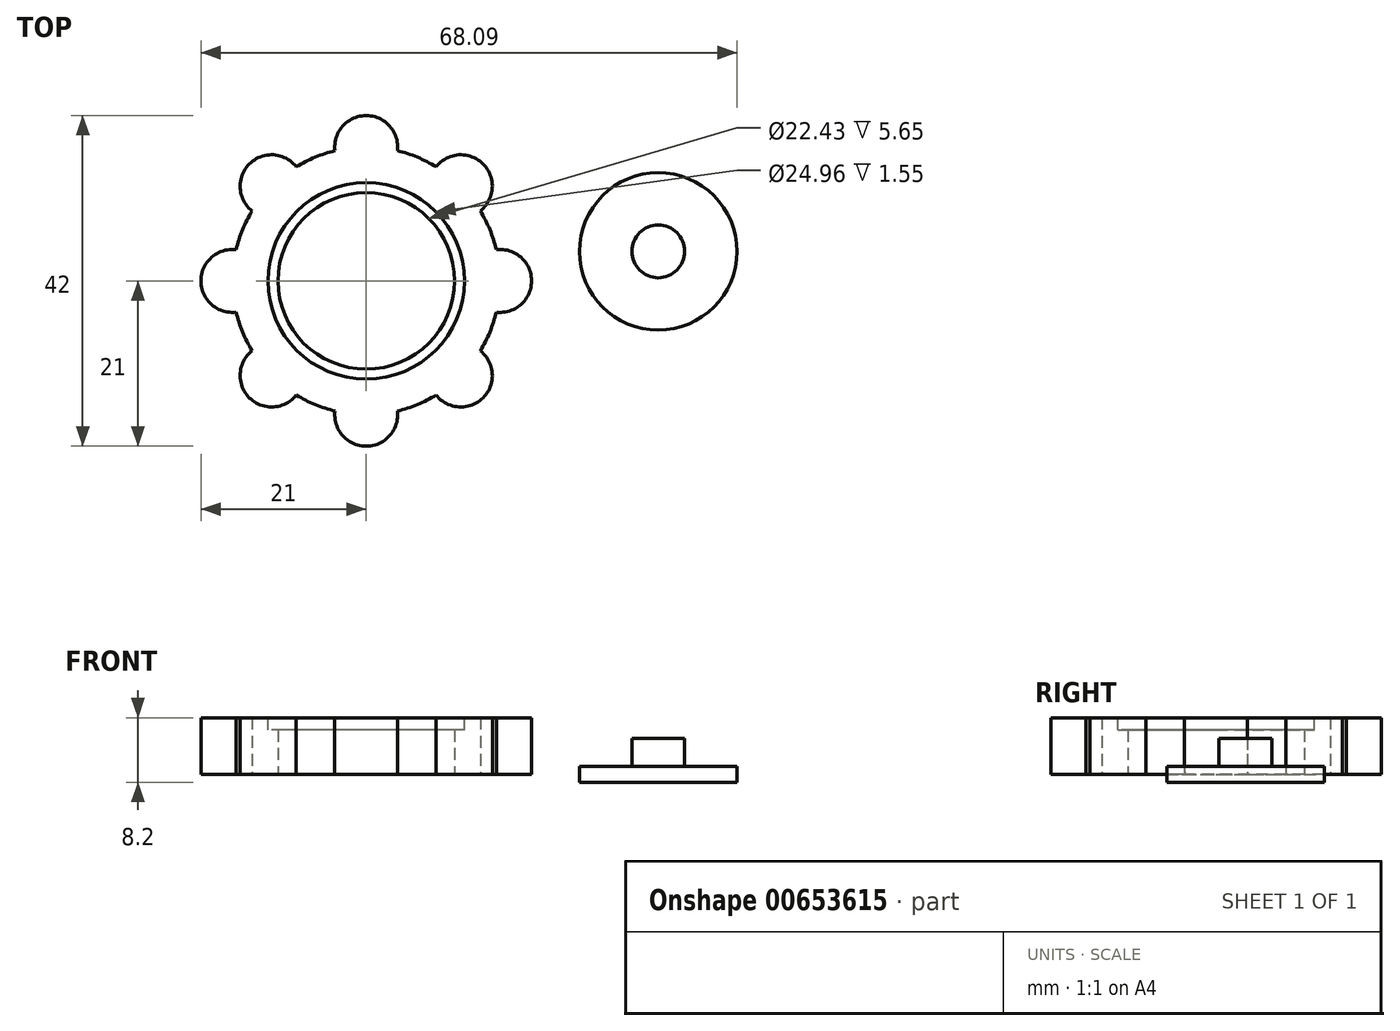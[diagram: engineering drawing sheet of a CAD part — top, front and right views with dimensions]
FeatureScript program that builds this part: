
annotation { "Feature Type Name" : "Feature", "Feature Type Description" : "" }
export const myFeature = defineFeature(function(context is Context, id is Id, definition is map)
    precondition{}
    {
        {
            var Q0;
            Q0=qCreatedBy(makeId("Top.planeOp"),FACE);
            var sketch = newSketch(context, id + "F0", { "sketchPlane" : qUnion([Q0])});
            skCircle(sketch, "E0", {"center": v(0, 0) * mm, "radius": 4.66 * mm});
            skCircle(sketch, "E1", {"center": v(0, 0) * mm, "radius": 11.21 * mm});
            skArc(sketch, "E2", {"start": v(-14.5, 8.88) * mm, "mid": v(-15.7, 6.5) * mm, "end": v(-16.53, 3.97) * mm});
            skArc(sketch, "E3", {"start": v(3.97, 16.53) * mm, "mid": v(0, 21) * mm, "end": v(-3.97, 16.53) * mm});
            skArc(sketch, "E4", {"start": v(-8.88, 14.5) * mm, "mid": v(-14.85, 14.85) * mm, "end": v(-14.5, 8.88) * mm});
            skArc(sketch, "E5", {"start": v(-16.53, 3.97) * mm, "mid": v(-21, 0) * mm, "end": v(-16.53, -3.97) * mm});
            skArc(sketch, "E6.MirrorC", {"start": v(-8.88, -14.5) * mm, "mid": v(-14.85, -14.85) * mm, "end": v(-14.5, -8.88) * mm});
            skArc(sketch, "E7.MirrorC", {"start": v(3.97, -16.53) * mm, "mid": v(0, -21) * mm, "end": v(-3.97, -16.53) * mm});
            skArc(sketch, "E8.MirrorC", {"start": v(8.88, 14.5) * mm, "mid": v(14.85, 14.85) * mm, "end": v(14.5, 8.88) * mm});
            skArc(sketch, "E9.MirrorC", {"start": v(16.53, 3.97) * mm, "mid": v(21, 0) * mm, "end": v(16.53, -3.97) * mm});
            skArc(sketch, "E10.MirrorC", {"start": v(8.88, -14.5) * mm, "mid": v(14.85, -14.85) * mm, "end": v(14.5, -8.88) * mm});
            skArc(sketch, "E11.trimOffspring", {"start": v(-16.53, -3.97) * mm, "mid": v(-15.7, -6.5) * mm, "end": v(-14.5, -8.88) * mm});
            skArc(sketch, "E12.trimOffspring", {"start": v(-8.88, -14.5) * mm, "mid": v(-6.5, -15.7) * mm, "end": v(-3.97, -16.53) * mm});
            skArc(sketch, "E13.trimOffspring", {"start": v(3.97, -16.53) * mm, "mid": v(6.5, -15.7) * mm, "end": v(8.88, -14.5) * mm});
            skArc(sketch, "E14.trimOffspring", {"start": v(14.5, -8.88) * mm, "mid": v(15.7, -6.5) * mm, "end": v(16.53, -3.97) * mm});
            skArc(sketch, "E15.trimOffspring", {"start": v(16.53, 3.97) * mm, "mid": v(15.7, 6.5) * mm, "end": v(14.5, 8.88) * mm});
            skArc(sketch, "E16.trimOffspring", {"start": v(8.88, 14.5) * mm, "mid": v(6.5, 15.7) * mm, "end": v(3.97, 16.53) * mm});
            skArc(sketch, "E17.trimOffspring", {"start": v(-3.97, 16.53) * mm, "mid": v(-6.5, 15.7) * mm, "end": v(-8.88, 14.5) * mm});
            skSolve(sketch);
        }
        {
            var Q0;
            Q0=makeQuery(id+"F0.imprint","IMPRINT",FACE,{"disambiguationData":[TD([[makeQuery(id+"F0.imprint","IMPRINT",EDGE,{"derivedFrom":sQuery(id+"F0.wireOp",EDGE,"E0")}),1.0]])]});
            var Q1;
            Q1=makeQuery(id+"F0.imprint","IMPRINT",FACE,{"disambiguationData":[TD([[makeQuery(id+"F0.imprint","IMPRINT",EDGE,{"derivedFrom":sQuery(id+"F0.wireOp",EDGE,"E1")}),-1.0]])]});
            extrude(context, id + "F1", {"entities" : qUnion([Q0, Q1]), "depth" : 7.2 * mm, "offsetDistance" : 25 * mm});
        }
        {
            var Q0;
            Q0=makeQuery(id+"F1.opExtrude","CAP_FACE",FACE,{"disambiguationData":[OSD([sQuery(id+"F0.wireOp",EDGE,"E1"),sQuery(id+"F0.wireOp",EDGE,"E2")])],"isStart":false});
            var sketch = newSketch(context, id + "F2", { "sketchPlane" : qUnion([Q0])});
            skCircle(sketch, "E18", {"center": v(0, 0) * mm, "radius": 12.48 * mm});
            skSolve(sketch);
        }
        {
            var Q0;
            Q0=makeQuery(id+"F2.imprint","IMPRINT",FACE,{"disambiguationData":[TD([[makeQuery(id+"F2.imprint","IMPRINT",EDGE,{"derivedFrom":sQuery(id+"F2.wireOp",EDGE,"E18")}),1.0]])]});
            extrude(context, id + "F3", {"entities" : qUnion([Q0]), "operationType" : NewBodyOperationType.REMOVE, "oppositeDirection" : true, "depth" : 1.55 * mm, "offsetDistance" : 25 * mm});
        }
        {
            var Q0;
            Q0=qCreatedBy(makeId("Top.planeOp"),FACE);
            var sketch = newSketch(context, id + "F4", { "sketchPlane" : qUnion([Q0])});
            skCircle(sketch, "E19", {"center": v(0, 0) * mm, "radius": 5.8 * mm});
            skSolve(sketch);
        }
        {
            var Q0;
            Q0 = qSketchRegion(id + "F4", true);
            extrude(context, id + "F5", {"entities" : qUnion([Q0]), "operationType" : NewBodyOperationType.ADD, "depth" : 1 * mm, "offsetDistance" : 25 * mm});
        }
        {
            var Q0;
            Q0=makeQuery(id+"F0.imprint","IMPRINT",FACE,{"disambiguationData":[TD([[makeQuery(id+"F0.imprint","IMPRINT",EDGE,{"derivedFrom":sQuery(id+"F0.wireOp",EDGE,"E0")}),1.0]])]});
            extrude(context, id + "F6", {"entities" : qUnion([Q0]), "operationType" : NewBodyOperationType.ADD, "depth" : 8.4 * mm, "offsetDistance" : 25 * mm});
        }
        {
            var Q0;
            Q0=makeQuery(id+"F6.opExtrude","CAP_FACE",FACE,{"disambiguationData":[OSD([sQuery(id+"F0.wireOp",EDGE,"E0")])],"isStart":false});
            var sketch = newSketch(context, id + "F7", { "sketchPlane" : qUnion([Q0])});
            skCircle(sketch, "E20", {"center": v(0, 0) * mm, "radius": 3.5 * mm});
            skSolve(sketch);
        }
        {
            var Q0;
            Q0=makeQuery(id+"F7.imprint","IMPRINT",FACE,{"disambiguationData":[TD([[makeQuery(id+"F7.imprint","IMPRINT",EDGE,{"derivedFrom":sQuery(id+"F7.wireOp",EDGE,"E20")}),1.0]])]});
            extrude(context, id + "F8", {"entities" : qUnion([Q0]), "operationType" : NewBodyOperationType.REMOVE, "oppositeDirection" : true, "depth" : 25 * mm, "offsetDistance" : 25 * mm});
        }
        {
            var Q0;
            Q0=qCreatedBy(makeId("Top.planeOp"),FACE);
            var sketch = newSketch(context, id + "F9", { "sketchPlane" : qUnion([Q0])});
            skCircle(sketch, "E21", {"center": v(37.1, 3.74) * mm, "radius": 10 * mm});
            skCircle(sketch, "E22", {"center": v(37.1, 3.74) * mm, "radius": 3.35 * mm});
            skSolve(sketch);
        }
        {
            var Q0;
            Q0=makeQuery(id+"F9.imprint","IMPRINT",FACE,{"disambiguationData":[TD([[makeQuery(id+"F9.imprint","IMPRINT",EDGE,{"derivedFrom":sQuery(id+"F9.wireOp",EDGE,"E21")}),1.0]])]});
            extrude(context, id + "F10", {"entities" : qUnion([Q0]), "depth" : 1 * mm, "offsetDistance" : 25 * mm});
        }
        {
            var Q0;
            Q0=makeQuery(id+"F9.imprint","IMPRINT",FACE,{"disambiguationData":[TD([[makeQuery(id+"F9.imprint","IMPRINT",EDGE,{"derivedFrom":sQuery(id+"F9.wireOp",EDGE,"E22")}),1.0]])]});
            extrude(context, id + "F11", {"entities" : qUnion([Q0]), "operationType" : NewBodyOperationType.ADD, "depth" : 4.6 * mm, "offsetDistance" : 25 * mm});
        }
        {
            var Q0;
            Q0=makeQuery(id+"F5.boolean.opBoolean","MERGE",FACE,{"derivedFrom":[makeQuery(id+"F1.opExtrude","CAP_FACE",FACE,{"disambiguationData":[OSD([sQuery(id+"F0.wireOp",EDGE,"E0")])],"isStart":true}),makeQuery(id+"F5.opExtrude","CAP_FACE",FACE,{"disambiguationData":[OSD([sQuery(id+"F4.wireOp",EDGE,"E19")])],"isStart":true})]});
            extrude(context, id + "F12", {"entities" : qUnion([Q0]), "operationType" : NewBodyOperationType.ADD, "depth" : 1 * mm, "offsetDistance" : 25 * mm});
        }
        {
            var Q0;
            Q0=makeQuery(id+"F9.imprint","IMPRINT",FACE,{"disambiguationData":[TD([[makeQuery(id+"F9.imprint","IMPRINT",EDGE,{"derivedFrom":sQuery(id+"F9.wireOp",EDGE,"E21")}),1.0]])]});
            var Q1;
            Q1=makeQuery(id+"F9.imprint","IMPRINT",FACE,{"disambiguationData":[TD([[makeQuery(id+"F9.imprint","IMPRINT",EDGE,{"derivedFrom":sQuery(id+"F9.wireOp",EDGE,"E22")}),1.0]])]});
            extrude(context, id + "F13", {"entities" : qUnion([Q0, Q1]), "operationType" : NewBodyOperationType.ADD, "oppositeDirection" : true, "depth" : 1 * mm, "offsetDistance" : 25 * mm});
        }
        {
            var Q0;
            Q0=makeQuery(id+"F1.opExtrude","SWEPT_BODY",BODY,{"disambiguationData":[OSD([sQuery(id+"F0.wireOp",EDGE,"E0")])]});
            deleteBodies(context, id + "F14", {"entities" : qUnion([Q0])});
        }
    });
